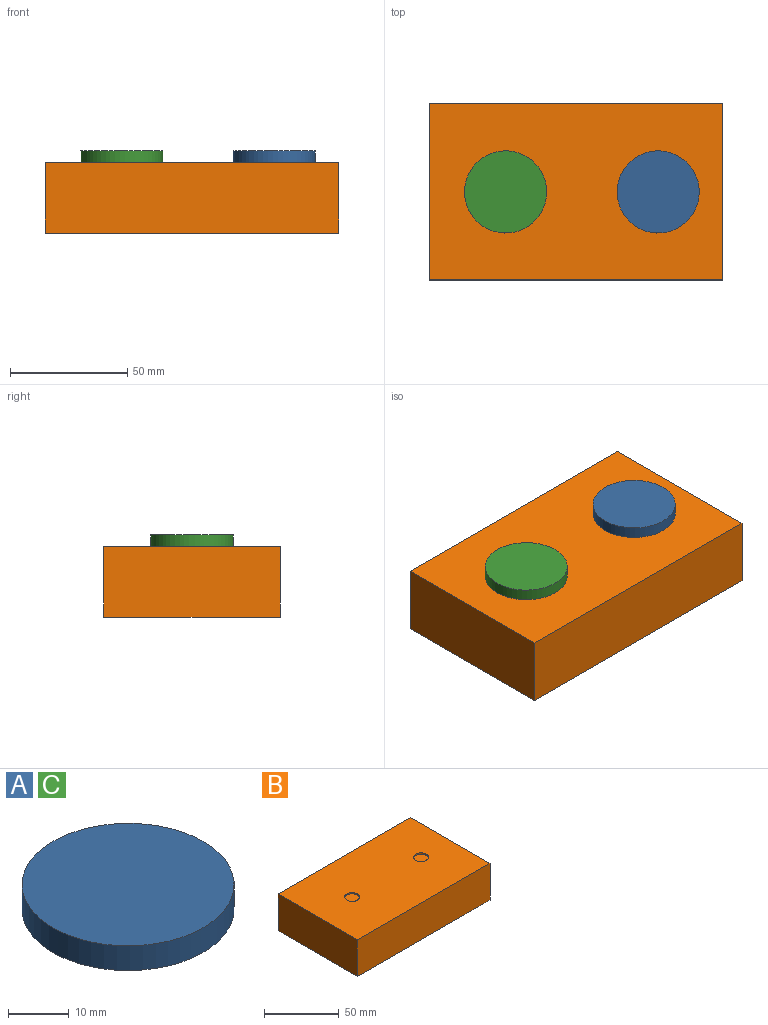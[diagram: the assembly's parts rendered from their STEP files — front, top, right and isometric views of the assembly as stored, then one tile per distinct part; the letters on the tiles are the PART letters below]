
ASSEMBLY  parts=3 mates=2
PART A: 3 faces, bbox 35x35x5 mm
  f0: cylinder r=17.5mm len=35mm, axis (0,0,-1), area 549.8mm2, adj f1,f2
  f1: plane 35x35mm, normal (0,0,1), area 962.1mm2, adj f0
  f2: plane 35x35mm, normal (0,0,-1), area 962.1mm2, adj f0
PART B: 10 faces, bbox 125x75x30 mm
  f0: plane 75x30mm, normal (-1,0,0), area 2250mm2, adj f1,f3,f4,f5
  f1: plane 125x30mm, normal (0,-1,0), area 3750mm2, adj f0,f2,f4,f5
  f2: plane 75x30mm, normal (1,0,0), area 2250mm2, adj f1,f3,f4,f5
  f3: plane 125x30mm, normal (0,1,0), area 3750mm2, adj f0,f2,f4,f5
  f4: plane 125x75mm, normal (0,0,1), area 9217.9mm2, adj f0,f1,f2,f3,f6,f8
  f5: plane 125x75mm, normal (0,0,-1), area 9375mm2, adj f0,f1,f2,f3
  f6: cylinder r=5mm len=10mm, axis (0,0,1), area 31.4mm2, adj f4,f7
  f7: plane 10x10mm, normal (0,0,1), area 78.5mm2, adj f6
  f8: cylinder r=5mm len=10mm, axis (0,0,1), area 31.4mm2, adj f4,f9
  f9: plane 10x10mm, normal (0,0,1), area 78.5mm2, adj f8
PART C: same geometry as A
PLACE A t=(18.87,1.41,-20.99)mm
PLACE B t=(-78.63,38.91,-50.99)mm
PLACE C t=(-46.13,1.41,-20.99)mm
MATE revolute A.f0 <-> B.f6  axis (0,0,-1) through (18.87,1.41,-20.99)mm
MATE revolute C.f0 <-> B.f8  axis (0,0,-1) through (-46.13,1.41,-20.99)mm
